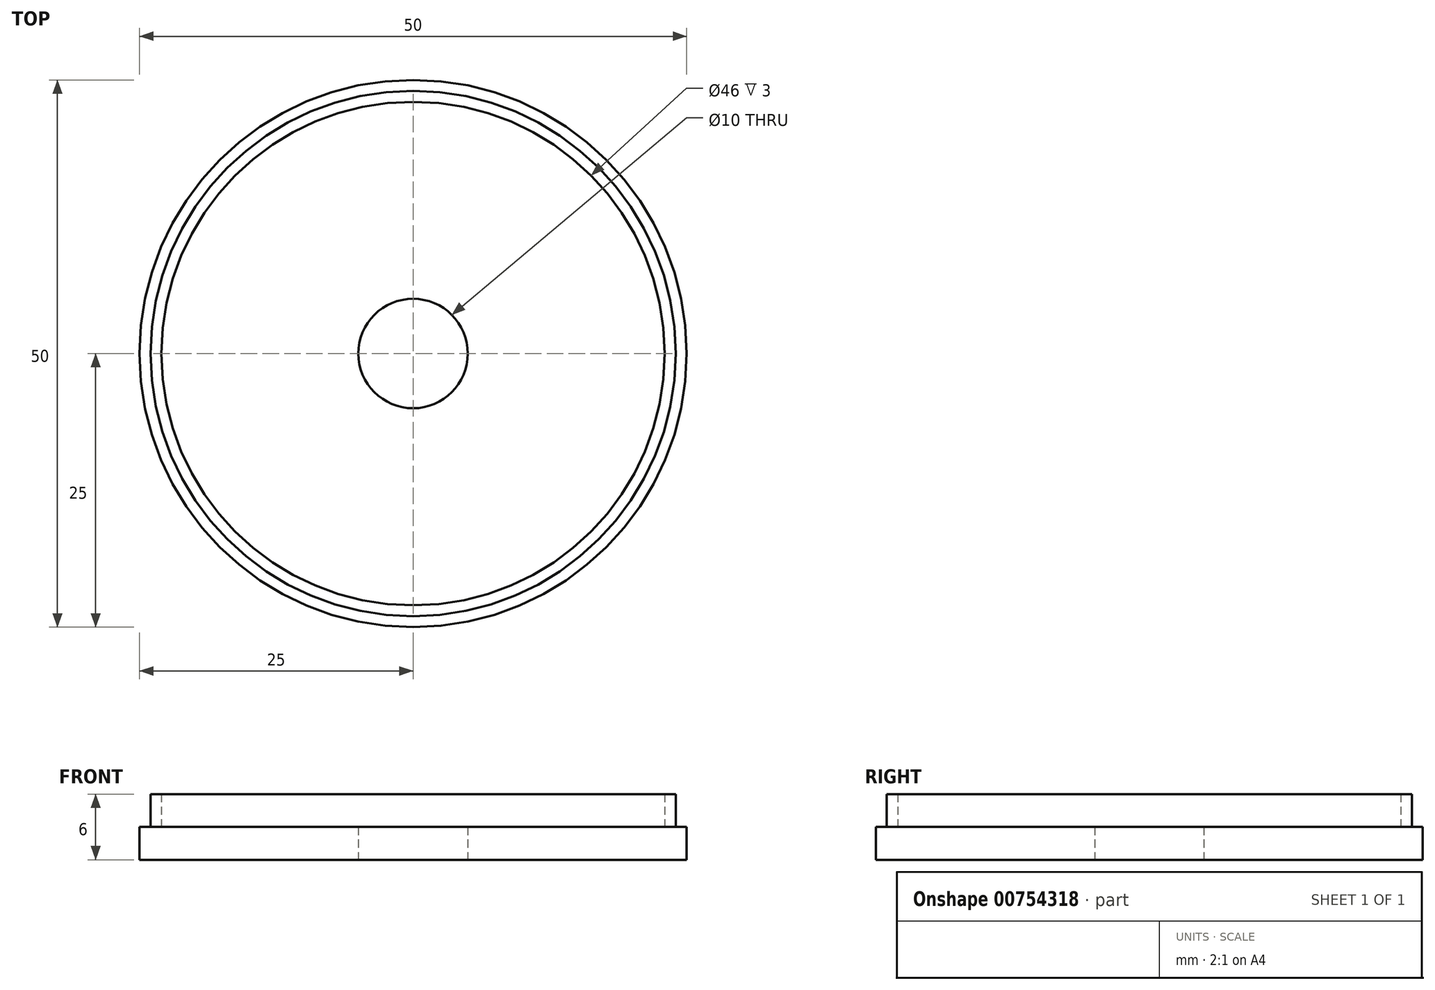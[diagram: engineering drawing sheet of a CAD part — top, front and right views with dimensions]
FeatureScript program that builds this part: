
annotation { "Feature Type Name" : "Feature", "Feature Type Description" : "" }
export const myFeature = defineFeature(function(context is Context, id is Id, definition is map)
    precondition{}
    {
        {
            var Q0;
            Q0=qCreatedBy(makeId("Top.planeOp"),FACE);
            var sketch = newSketch(context, id + "F0", { "sketchPlane" : qUnion([Q0])});
            skCircle(sketch, "E0", {"center": v(0, 0) * mm, "radius": 25 * mm});
            skSolve(sketch);
        }
        {
            var Q0;
            Q0 = qSketchRegion(id + "F0", true);
            extrude(context, id + "F1", {"entities" : qUnion([Q0]), "depth" : 3 * mm, "offsetDistance" : 25 * mm});
        }
        {
            var Q0;
            Q0=makeQuery(id+"F1.opExtrude","CAP_FACE",FACE,{"disambiguationData":[OSD([sQuery(id+"F0.wireOp",EDGE,"E0")])],"isStart":false});
            var sketch = newSketch(context, id + "F2", { "sketchPlane" : qUnion([Q0])});
            skCircle(sketch, "E1", {"center": v(0, 0) * mm, "radius": 24 * mm});
            skCircle(sketch, "E2", {"center": v(0, 0) * mm, "radius": 23 * mm});
            skSolve(sketch);
        }
        {
            var Q0;
            Q0 = qSketchRegion(id + "F2", true);
            extrude(context, id + "F3", {"entities" : qUnion([Q0]), "operationType" : NewBodyOperationType.ADD, "depth" : 3 * mm, "offsetDistance" : 25 * mm});
        }
        {
            var Q0;
            Q0=sQuery(id+"F0.wireOp",VERTEX,"E0.center");
            var Q1;
            Q1=makeQuery(id+"F1.opExtrude","SWEPT_BODY",BODY,{"disambiguationData":[OSD([sQuery(id+"F0.wireOp",EDGE,"E0")])]});
            hole(context, id + "F4", {"style" : HoleStyle.SIMPLE, "endStyle" : HoleEndStyle.THROUGH, "oppositeDirection" : true, "holeDiameter" : 10 * mm, "majorDiameter" : 5 * mm, "isTappedThrough" : true, "tappedDepth" : 12 * mm, "tapClearance" : 3, "locations" : qUnion([Q0]), "scope" : qUnion([Q1])});
        }
    });
